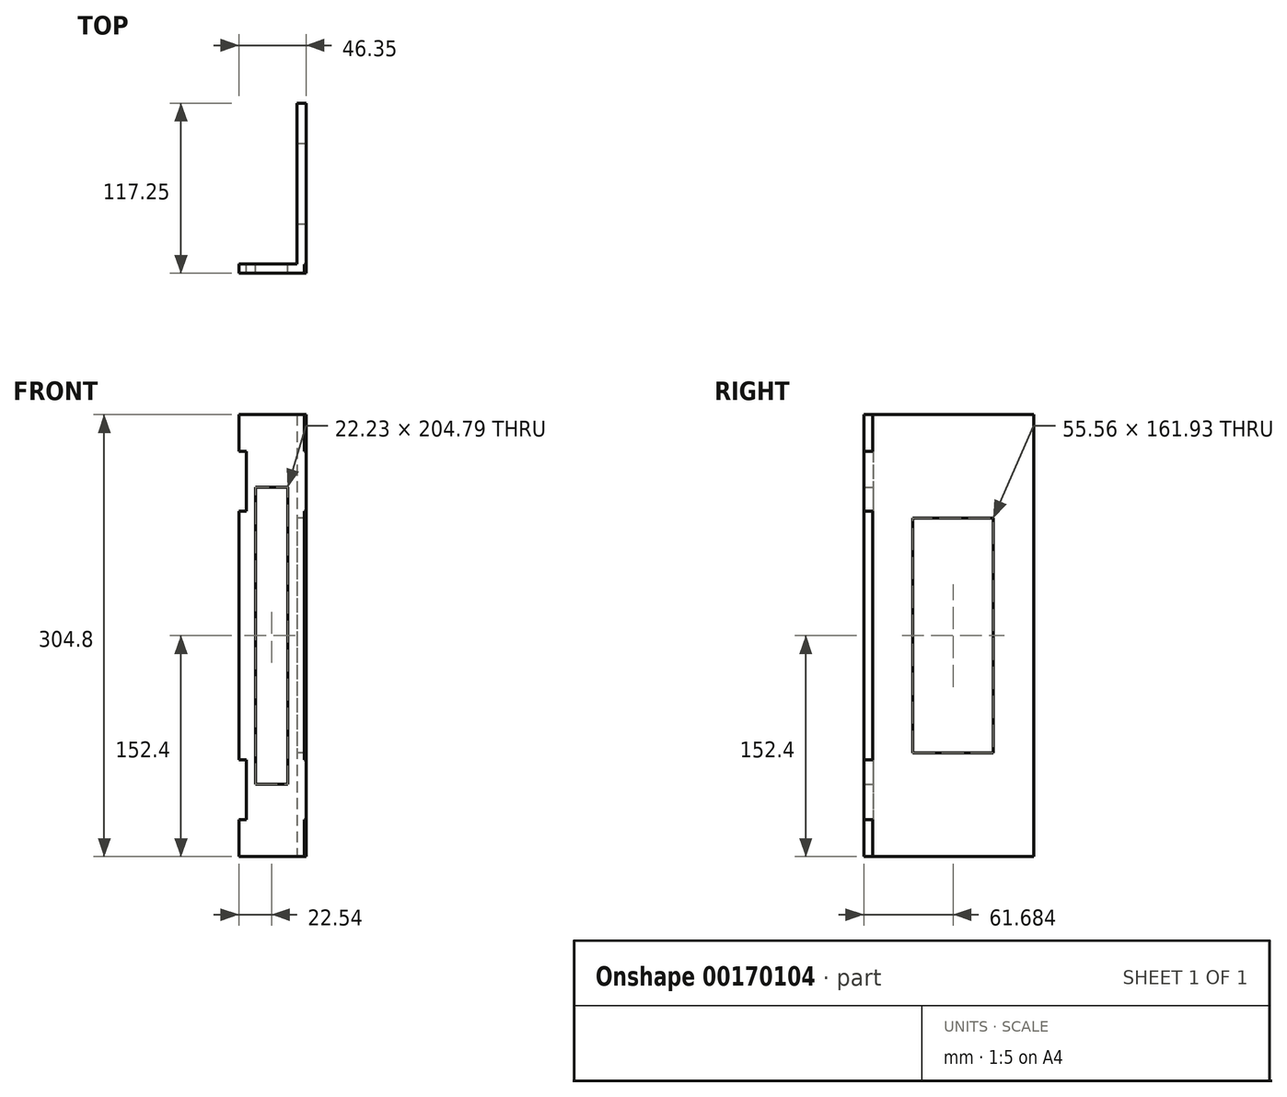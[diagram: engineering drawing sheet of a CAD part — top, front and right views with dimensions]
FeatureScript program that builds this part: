
annotation { "Feature Type Name" : "Feature", "Feature Type Description" : "" }
export const myFeature = defineFeature(function(context is Context, id is Id, definition is map)
    precondition{}
    {
        {
            var Q0;
            Q0=qCreatedBy(makeId("Front.planeOp"),FACE);
            var sketch = newSketch(context, id + "F0", { "sketchPlane" : qUnion([Q0])});
            skLineSegment(sketch, "E0.bottom", {"start": v(-7.94, 85.73) * mm, "end": v(7.94, 85.73) * mm});
            skLineSegment(sketch, "E0.top", {"start": v(-7.94, -85.73) * mm, "end": v(7.94, -85.73) * mm});
            skLineSegment(sketch, "E0.left", {"start": v(-7.94, 85.73) * mm, "end": v(-7.94, -85.73) * mm});
            skLineSegment(sketch, "E0.right", {"start": v(7.94, 85.73) * mm, "end": v(7.94, -85.73) * mm});
            skPoint(sketch, "E0.middle", {"position": v(0, 0) * mm});
            skLineSegment(sketch, "E1.bottom", {"start": v(-11.11, 102.4) * mm, "end": v(11.11, 102.4) * mm});
            skLineSegment(sketch, "E1.top", {"start": v(-11.11, -102.4) * mm, "end": v(11.11, -102.4) * mm});
            skLineSegment(sketch, "E1.left", {"start": v(-11.11, 102.4) * mm, "end": v(-11.11, -102.4) * mm});
            skLineSegment(sketch, "E1.right", {"start": v(11.11, 102.4) * mm, "end": v(11.11, -102.4) * mm});
            skCircle(sketch, "E2", {"center": v(0, 90.49) * mm, "radius": 1.2 * mm});
            skCircle(sketch, "E3.MirrorC", {"center": v(0, -90.49) * mm, "radius": 1.2 * mm});
            skLineSegment(sketch, "E4.bottom", {"start": v(-17.46, 152.4) * mm, "end": v(17.46, 152.4) * mm});
            skLineSegment(sketch, "E4.top", {"start": v(-17.46, -152.4) * mm, "end": v(17.46, -152.4) * mm});
            skLineSegment(sketch, "E4.left", {"start": v(-17.46, 127) * mm, "end": v(-17.46, 85.73) * mm});
            skLineSegment(sketch, "E4.right", {"start": v(17.46, 127) * mm, "end": v(17.46, 85.73) * mm});
            skLineSegment(sketch, "E5.bottom", {"start": v(-17.46, 152.4) * mm, "end": v(-22.54, 152.4) * mm});
            skLineSegment(sketch, "E5.right", {"start": v(-22.54, 152.4) * mm, "end": v(-22.54, 127) * mm});
            skLineSegment(sketch, "E6.bottom", {"start": v(-22.54, 127) * mm, "end": v(-17.46, 127) * mm});
            skLineSegment(sketch, "E6.top", {"start": v(-22.54, 85.73) * mm, "end": v(-17.46, 85.73) * mm});
            skLineSegment(sketch, "E7.trimOffspring", {"start": v(-22.54, 85.73) * mm, "end": v(-22.54, 0) * mm});
            skLineSegment(sketch, "E8.MirrorCS", {"start": v(-22.54, -85.73) * mm, "end": v(-22.54, 0) * mm});
            skLineSegment(sketch, "E9.MirrorCS", {"start": v(-22.54, -85.73) * mm, "end": v(-17.46, -85.73) * mm});
            skLineSegment(sketch, "E10.MirrorCS", {"start": v(-17.46, -152.4) * mm, "end": v(-22.54, -152.4) * mm});
            skLineSegment(sketch, "E11.MirrorCS", {"start": v(-22.54, -152.4) * mm, "end": v(-22.54, -127) * mm});
            skLineSegment(sketch, "E12.MirrorCS", {"start": v(-22.54, -127) * mm, "end": v(-17.46, -127) * mm});
            skLineSegment(sketch, "E13.MirrorCS", {"start": v(17.46, -152.4) * mm, "end": v(22.54, -152.4) * mm});
            skLineSegment(sketch, "E14.MirrorCS", {"start": v(22.54, -152.4) * mm, "end": v(22.54, -127) * mm});
            skLineSegment(sketch, "E15.MirrorCS", {"start": v(22.54, -127) * mm, "end": v(17.46, -127) * mm});
            skLineSegment(sketch, "E16.MirrorCS", {"start": v(22.54, -85.73) * mm, "end": v(17.46, -85.73) * mm});
            skLineSegment(sketch, "E17.MirrorCS", {"start": v(22.54, -85.73) * mm, "end": v(22.54, 0) * mm});
            skLineSegment(sketch, "E18.MirrorCS", {"start": v(22.54, 85.73) * mm, "end": v(22.54, 0) * mm});
            skLineSegment(sketch, "E19.MirrorCS", {"start": v(22.54, 85.73) * mm, "end": v(17.46, 85.73) * mm});
            skLineSegment(sketch, "E20.MirrorCS", {"start": v(22.54, 127) * mm, "end": v(17.46, 127) * mm});
            skLineSegment(sketch, "E21.MirrorCS", {"start": v(17.46, 152.4) * mm, "end": v(22.54, 152.4) * mm});
            skLineSegment(sketch, "E22.MirrorCS", {"start": v(22.54, 152.4) * mm, "end": v(22.54, 127) * mm});
            skLineSegment(sketch, "E23.trimOffspring", {"start": v(-17.46, -85.73) * mm, "end": v(-17.46, -127) * mm});
            skLineSegment(sketch, "E24.trimOffspring", {"start": v(17.46, -85.72) * mm, "end": v(17.46, -127) * mm});
            skSolve(sketch);
        }
        {
            var Q0;
            Q0=makeQuery(id+"F0.imprint","IMPRINT",FACE,{"disambiguationData":[TD([[makeQuery(id+"F0.imprint","IMPRINT",EDGE,{"derivedFrom":sQuery(id+"F0.wireOp",EDGE,"E1.bottom")}),1.0]])]});
            extrude(context, id + "F1", {"entities" : qUnion([Q0]), "depth" : 6.35 * mm});
        }
        {
            var Q0;
            Q0=qCreatedBy(makeId("Right.planeOp"),FACE);
            cPlane(context, id + "F2", {"entities" : qUnion([Q0]), "cplaneType" : CPlaneType.OFFSET, "offset" : 17.46 * mm, "width" : 152.4 * mm, "height" : 152.4 * mm});
        }
        {
            var Q0;
            Q0=qCreatedBy(id+"F2.planeOp",FACE);
            var sketch = newSketch(context, id + "F3", { "sketchPlane" : qUnion([Q0])});
            skLineSegment(sketch, "E25", {"start": v(55.33, 146.13) * mm, "end": v(55.33, -156.26) * mm, "construction": true});
            skLineSegment(sketch, "E26.bottom", {"start": v(27.55, 80.96) * mm, "end": v(83.12, 80.96) * mm});
            skLineSegment(sketch, "E26.top", {"start": v(27.55, -80.96) * mm, "end": v(83.12, -80.96) * mm});
            skLineSegment(sketch, "E26.left", {"start": v(27.55, 80.96) * mm, "end": v(27.55, -80.96) * mm});
            skLineSegment(sketch, "E26.right", {"start": v(83.12, 80.96) * mm, "end": v(83.12, -80.96) * mm});
            skPoint(sketch, "E26.middle", {"position": v(55.33, 0) * mm});
            skCircle(sketch, "E27", {"center": v(55.33, 20.64) * mm, "radius": 19.05 * mm});
            skLineSegment(sketch, "E28.bottom", {"start": v(110.9, 152.4) * mm, "end": v(-0.23, 152.4) * mm});
            skLineSegment(sketch, "E28.top", {"start": v(110.9, -152.4) * mm, "end": v(-0.23, -152.4) * mm});
            skLineSegment(sketch, "E28.left", {"start": v(110.9, 152.4) * mm, "end": v(110.9, -152.4) * mm});
            skLineSegment(sketch, "E28.right", {"start": v(-0.23, 152.4) * mm, "end": v(-0.23, 127) * mm});
            skLineSegment(sketch, "E29.0", {"start": v(-6.35, 127) * mm, "end": v(0, 127) * mm});
            skLineSegment(sketch, "E30.0", {"start": v(-6.35, 85.73) * mm, "end": v(0, 85.73) * mm});
            skLineSegment(sketch, "E31.0", {"start": v(-6.35, -85.73) * mm, "end": v(0, -85.73) * mm});
            skLineSegment(sketch, "E32.0", {"start": v(-6.35, -127) * mm, "end": v(0, -127) * mm});
            skPoint(sketch, "E33.0", {"position": v(-3.18, -152.4) * mm});
            skLineSegment(sketch, "E34.0", {"start": v(-6.35, 127) * mm, "end": v(-6.35, 85.73) * mm});
            skLineSegment(sketch, "E35.trimOffspring", {"start": v(-0.23, 85.72) * mm, "end": v(-0.23, -85.73) * mm});
            skLineSegment(sketch, "E36.0", {"start": v(-6.35, -85.72) * mm, "end": v(-6.35, -127) * mm});
            skLineSegment(sketch, "E37.trimOffspring", {"start": v(-0.23, -127) * mm, "end": v(-0.23, -152.4) * mm});
            skSolve(sketch);
        }
        {
            var Q0;
            Q0=qSketchRegion(id+"F3",true);
            extrude(context, id + "F4", {"entities" : qUnion([Q0]), "operationType" : NewBodyOperationType.ADD, "depth" : 6.35 * mm});
        }
    });
